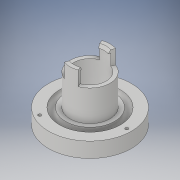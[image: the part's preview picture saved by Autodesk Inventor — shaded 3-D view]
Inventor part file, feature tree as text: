
AUTODESK INVENTOR PART (.ipt)
format: ipt  version: 2019 (Build 230136000, 136)  size: 194,048 bytes
history: native  units: mm
features: sketch x6, extrude x4, revolve x2
ambient origin geometry x8: Origin, YZ Plane, XZ Plane, XY Plane, X Axis, Y Axis, Z Axis, Center Point
bodies: Solid1 (feature_tree)
feature tree (12):
  extrude  "Extrusion1"  Depth=110.0mm
  revolve  "Revolution1"  [1 undecoded]
  extrude  "Extrusion2"  TaperAngle=90.0deg  [1 undecoded]
  revolve  "Revolution2"  [1 undecoded]
  extrude  "Extrusion3"  Depth=43.0mm
  extrude  "Extrusion4"  Depth=19.0mm
  sketch  "Sketch1"  dims[d0=43.0mm d1=110.0mm]
  sketch  "Sketch2"  dims[d2=20.0mm d3=0.0mm d4=10.0mm]
  sketch  "Sketch3"  dims[d5=15.0mm d6=90.0deg]
  sketch  "Sketch4"  dims[d7=60.0mm d8=0.0mm d9=2.5mm]
  sketch  "Sketch5"  dims[d10=90.0deg d18=43.0mm]
  sketch  "Sketch6"  dims[d19=43.0mm d20=53.0mm d22=6.981317mm d23=6.981317mm d24=3.490659mm d25=3.490659mm d26=24.43461mm d27=24.43461mm d28=19.0mm d29=0.0mm d30=30.0mm d32=360.0deg d34=18.0mm d35=0.0mm]
note: 3 required parameter values undecoded (feature->parameter linkage not recoverable at this tier; creation-order binding heuristic only, values carry confidence <= 0.55)